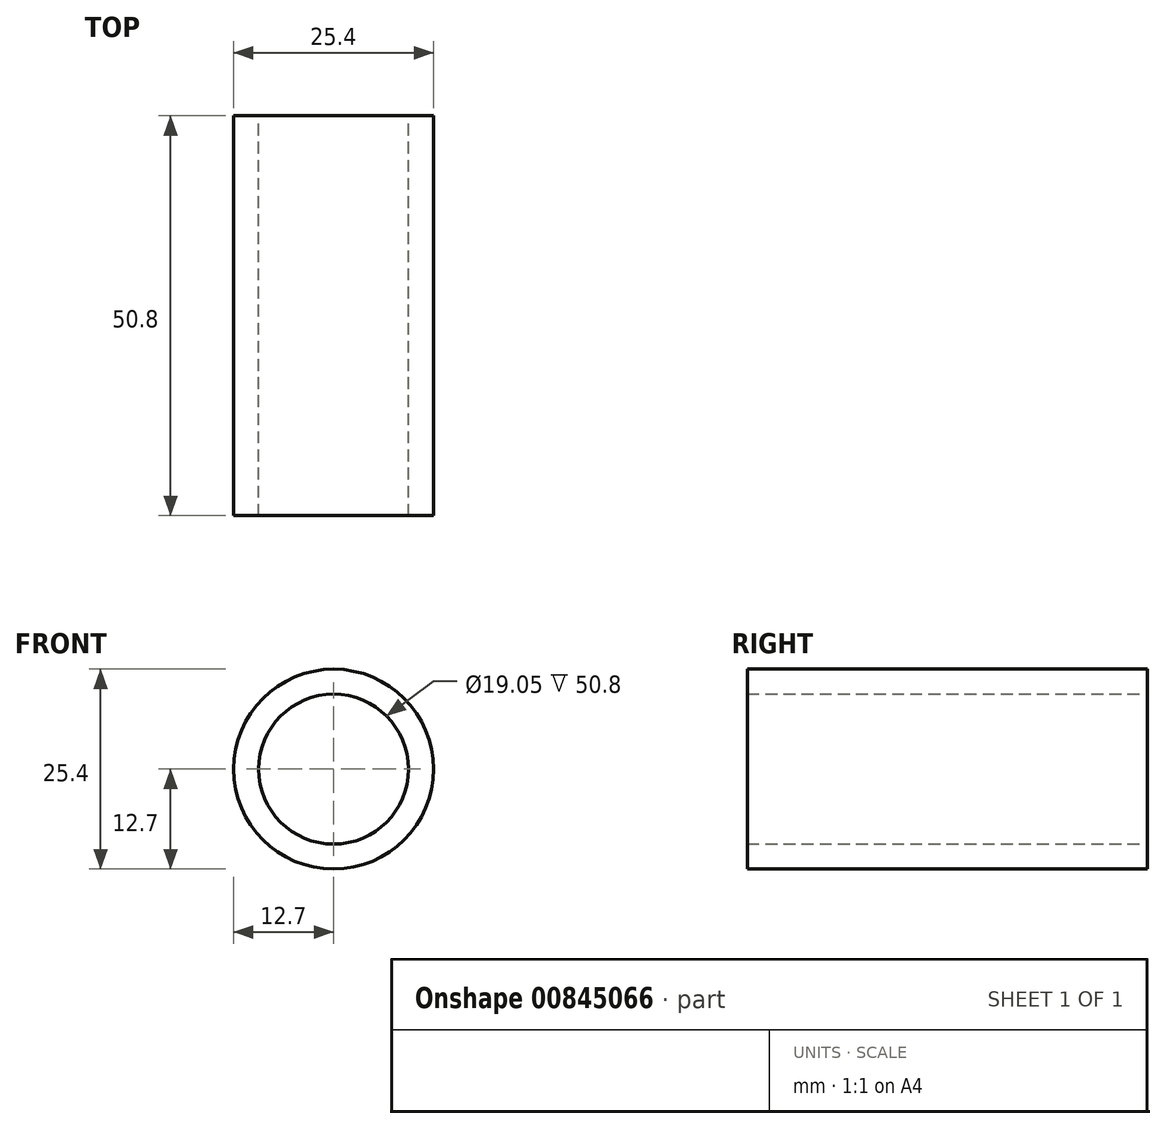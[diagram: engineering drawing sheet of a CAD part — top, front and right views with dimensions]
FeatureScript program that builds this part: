
annotation { "Feature Type Name" : "Feature", "Feature Type Description" : "" }
export const myFeature = defineFeature(function(context is Context, id is Id, definition is map)
    precondition{}
    {
        {
            var Q0;
            Q0=qCreatedBy(makeId("Front.planeOp"),FACE);
            var sketch = newSketch(context, id + "F0", { "sketchPlane" : qUnion([Q0])});
            skCircle(sketch, "E0", {"center": v(0, 0) * mm, "radius": 12.7 * mm});
            skCircle(sketch, "E1", {"center": v(0, 0) * mm, "radius": 9.53 * mm});
            skSolve(sketch);
        }
        {
            var Q0;
            Q0 = qSketchRegion(id + "F0", true);
            extrude(context, id + "F1", {"entities" : qUnion([Q0]), "depth" : 25.4 * mm, "offsetDistance" : 25.4 * mm, "hasSecondDirection" : true, "secondDirectionOppositeDirection" : true, "secondDirectionDepth" : 25.4 * mm});
        }
    });
